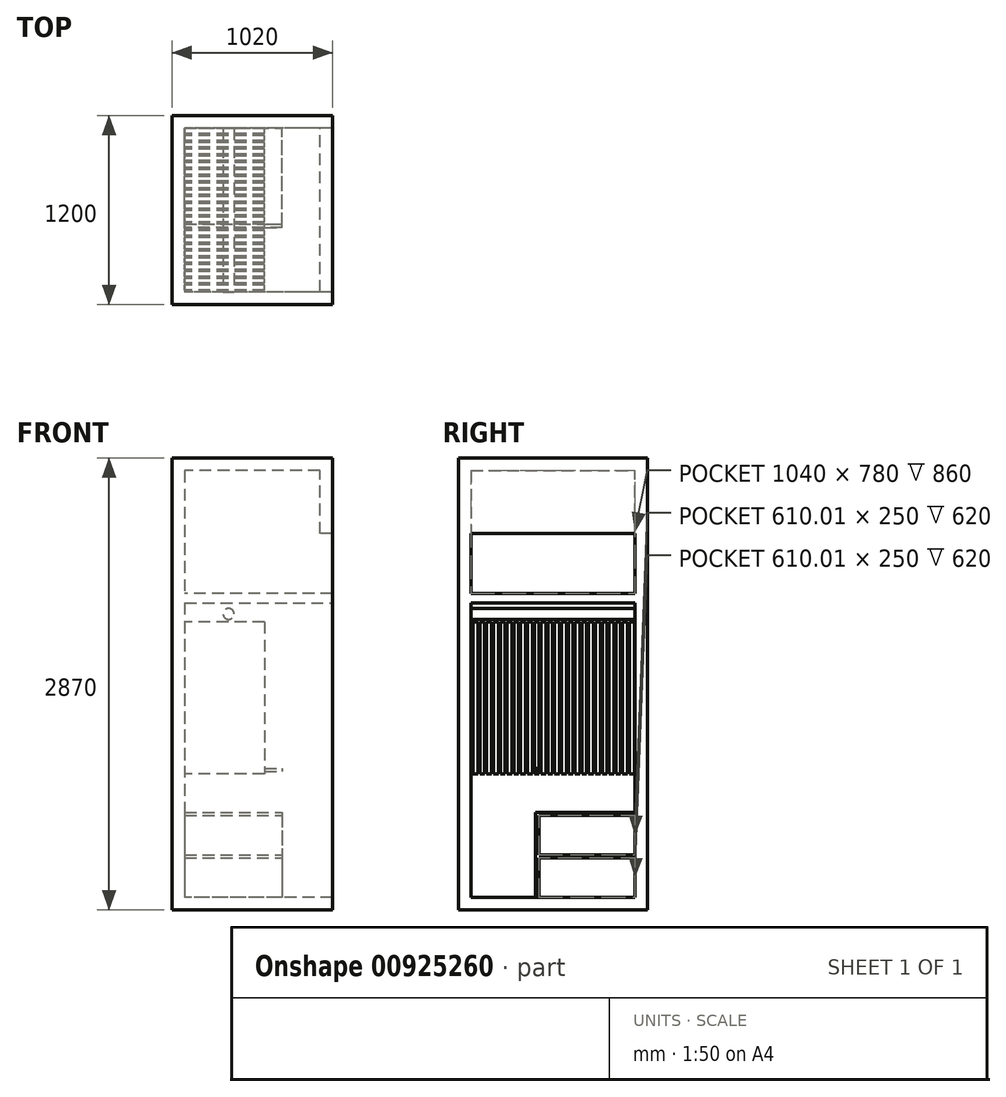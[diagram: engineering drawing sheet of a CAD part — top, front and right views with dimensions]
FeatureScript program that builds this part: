
annotation { "Feature Type Name" : "Feature", "Feature Type Description" : "" }
export const myFeature = defineFeature(function(context is Context, id is Id, definition is map)
    precondition{}
    {
        {
            var Q0;
            Q0=qCreatedBy(makeId("Top.planeOp"),FACE);
            var sketch = newSketch(context, id + "F0", { "sketchPlane" : qUnion([Q0])});
            skLineSegment(sketch, "E0.bottom", {"start": v(510, 600) * mm, "end": v(-510, 600) * mm});
            skLineSegment(sketch, "E0.top", {"start": v(510, -600) * mm, "end": v(-510, -600) * mm});
            skLineSegment(sketch, "E0.left", {"start": v(510, 600) * mm, "end": v(510, -600) * mm});
            skLineSegment(sketch, "E0.right", {"start": v(-510, 600) * mm, "end": v(-510, -600) * mm});
            skPoint(sketch, "E0.middle", {"position": v(0, 0) * mm});
            skSolve(sketch);
        }
        {
            var Q0;
            Q0=makeQuery(id+"F0.imprint","IMPRINT",FACE,{"disambiguationData":[TD([[makeQuery(id+"F0.imprint","IMPRINT",EDGE,{"derivedFrom":sQuery(id+"F0.wireOp",EDGE,"E0.bottom")}),1.0]])]});
            extrude(context, id + "F1", {"entities" : qUnion([Q0]), "depth" : 2870 * mm, "offsetDistance" : 25.4 * mm});
        }
        {
            var Q0;
            Q0=makeQuery(id+"F1.opExtrude","SWEPT_FACE",FACE,{"disambiguationData":[OSD([sQuery(id+"F0.wireOp",EDGE,"E0.left")])]});
            shell(context, id + "F2", {"entities" : qUnion([Q0]), "thickness" : 80 * mm});
        }
        {
            var Q0;
            {var subQ0=sQuery(id+"F0.wireOp",EDGE,"E0.right");var subQ1=sQuery(id+"F0.wireOp",EDGE,"E0.left");var subQ2=sQuery(id+"F0.wireOp",EDGE,"E0.top");var subQ3=sQuery(id+"F0.wireOp",EDGE,"E0.bottom");Q0=makeQuery(id+"F2.opShell","OFFSET_FACE",FACE,{"disambiguationData":[OSD([subQ3,subQ2,subQ1,subQ0]),TDD([makeQuery(id+"F1.opExtrude","CAP_FACE",FACE,{"disambiguationData":[OSD([subQ3,subQ2,subQ1,subQ0])],"isStart":false})])]});}
            var sketch = newSketch(context, id + "F3", { "sketchPlane" : qUnion([Q0])});
            skLineSegment(sketch, "E1.bottom", {"start": v(510, 520) * mm, "end": v(430, 520) * mm});
            skLineSegment(sketch, "E1.top", {"start": v(510, -520) * mm, "end": v(430, -520) * mm});
            skLineSegment(sketch, "E1.left", {"start": v(510, 520) * mm, "end": v(510, -520) * mm});
            skLineSegment(sketch, "E1.right", {"start": v(430, 520) * mm, "end": v(430, -520) * mm});
            skSolve(sketch);
        }
        {
            var Q0;
            Q0=makeQuery(id+"F3.imprint","IMPRINT",FACE,{"disambiguationData":[TD([[makeQuery(id+"F3.imprint","IMPRINT",EDGE,{"derivedFrom":sQuery(id+"F3.wireOp",EDGE,"E1.bottom")}),1.0]])]});
            extrude(context, id + "F4", {"entities" : qUnion([Q0]), "operationType" : NewBodyOperationType.ADD, "depth" : 400 * mm, "offsetDistance" : 25.4 * mm});
        }
        {
            var Q0;
            Q0=makeQuery(id+"F2.opShell","OFFSET_FACE",FACE,{"disambiguationData":[OSD([sQuery(id+"F0.wireOp",EDGE,"E0.top")])]});
            var sketch = newSketch(context, id + "F5", { "sketchPlane" : qUnion([Q0])});
            skLineSegment(sketch, "E2", {"start": v(-510, 2010) * mm, "end": v(430, 2010) * mm});
            skLineSegment(sketch, "E3", {"start": v(430, 2010) * mm, "end": v(430, 1950) * mm});
            skLineSegment(sketch, "E4", {"start": v(430, 1950) * mm, "end": v(-510, 1950) * mm});
            skLineSegment(sketch, "E5", {"start": v(-510, 1950) * mm, "end": v(-510, 2010) * mm});
            skSolve(sketch);
        }
        {
            var Q0;
            Q0=makeQuery(id+"F5.imprint","IMPRINT",FACE,{"disambiguationData":[TD([[makeQuery(id+"F5.imprint","IMPRINT",EDGE,{"derivedFrom":sQuery(id+"F5.wireOp",EDGE,"E2")}),-1.0]])]});
            extrude(context, id + "F6", {"entities" : qUnion([Q0]), "operationType" : NewBodyOperationType.ADD, "depth" : 1066.8 * mm, "offsetDistance" : 25.4 * mm});
        }
        {
            var Q0;
            {var subQ3=sQuery(id+"F0.wireOp",EDGE,"E0.bottom");Q0=makeQuery(id+"F6.boolean.opBoolean","SPLIT",FACE,{"disambiguationData":[TD([makeQuery(id+"F6.opExtrude","SWEPT_FACE",FACE,{"disambiguationData":[OSD([sQuery(id+"F5.wireOp",EDGE,"E4")])]})])],"derivedFrom":makeQuery(id+"F2.opShell","OFFSET_FACE",FACE,{"disambiguationData":[OSD([subQ3])]})});}
            var sketch = newSketch(context, id + "F7", { "sketchPlane" : qUnion([Q0])});
            skLineSegment(sketch, "E6.bottom", {"start": v(-430, 900) * mm, "end": v(190, 900) * mm});
            skLineSegment(sketch, "E6.top", {"start": v(-430, 80) * mm, "end": v(190, 80) * mm});
            skLineSegment(sketch, "E6.left", {"start": v(-430, 900) * mm, "end": v(-430, 80) * mm});
            skLineSegment(sketch, "E6.right", {"start": v(190, 900) * mm, "end": v(190, 80) * mm});
            skSolve(sketch);
        }
        {
            var Q0;
            Q0=makeQuery(id+"F7.imprint","IMPRINT",FACE,{"disambiguationData":[TD([[makeQuery(id+"F7.imprint","IMPRINT",EDGE,{"derivedFrom":sQuery(id+"F7.wireOp",EDGE,"E6.bottom")}),-1.0]])]});
            extrude(context, id + "F8", {"entities" : qUnion([Q0]), "operationType" : NewBodyOperationType.ADD, "depth" : 630 * mm, "offsetDistance" : 25.4 * mm});
        }
        {
            var Q0;
            Q0=makeQuery(id+"F8.opExtrude","SWEPT_FACE",FACE,{"disambiguationData":[OSD([sQuery(id+"F7.wireOp",EDGE,"E6.right")])]});
            var sketch = newSketch(context, id + "F9", { "sketchPlane" : qUnion([Q0])});
            skLineSegment(sketch, "E7.bottom", {"start": v(-110, 880) * mm, "end": v(520, 880) * mm});
            skLineSegment(sketch, "E7.top", {"start": v(-110, 620) * mm, "end": v(520, 620) * mm});
            skLineSegment(sketch, "E7.left", {"start": v(-110, 880) * mm, "end": v(-110, 620) * mm});
            skLineSegment(sketch, "E7.right", {"start": v(520, 880) * mm, "end": v(520, 620) * mm});
            skLineSegment(sketch, "E8.bottom", {"start": v(-110, 600) * mm, "end": v(520, 600) * mm});
            skLineSegment(sketch, "E8.top", {"start": v(-110, 350) * mm, "end": v(520, 350) * mm});
            skLineSegment(sketch, "E8.left", {"start": v(-110, 600) * mm, "end": v(-110, 350) * mm});
            skLineSegment(sketch, "E8.right", {"start": v(520, 600) * mm, "end": v(520, 350) * mm});
            skLineSegment(sketch, "E9.bottom", {"start": v(-110, 330) * mm, "end": v(520, 330) * mm});
            skLineSegment(sketch, "E9.top", {"start": v(-110, 80) * mm, "end": v(520, 80) * mm});
            skLineSegment(sketch, "E9.left", {"start": v(-110, 330) * mm, "end": v(-110, 80) * mm});
            skLineSegment(sketch, "E9.right", {"start": v(520, 330) * mm, "end": v(520, 80) * mm});
            skLineSegment(sketch, "E10", {"start": v(-90.01, 900) * mm, "end": v(-90.01, 80) * mm});
            skSolve(sketch);
        }
        {
            var Q0;
            {var subQ0=sQuery(id+"F9.wireOp",EDGE,"E7.right");Q0=makeQuery(id+"F9.imprint","IMPRINT",FACE,{"disambiguationData":[TD([[makeQuery(id+"F9.imprint","IMPRINT",EDGE,{"derivedFrom":subQ0}),-1.0]])]});}
            var Q1;
            {var subQ0=sQuery(id+"F9.wireOp",EDGE,"E8.right");Q1=makeQuery(id+"F9.imprint","IMPRINT",FACE,{"disambiguationData":[TD([[makeQuery(id+"F9.imprint","IMPRINT",EDGE,{"derivedFrom":subQ0}),-1.0]])]});}
            var Q2;
            {var subQ0=sQuery(id+"F9.wireOp",EDGE,"E9.right");Q2=makeQuery(id+"F9.imprint","IMPRINT",FACE,{"disambiguationData":[TD([[makeQuery(id+"F9.imprint","IMPRINT",EDGE,{"derivedFrom":subQ0}),-1.0]])]});}
            extrude(context, id + "F10", {"entities" : qUnion([Q0, Q1, Q2]), "operationType" : NewBodyOperationType.REMOVE, "oppositeDirection" : true, "depth" : 620 * mm, "offsetDistance" : 25.4 * mm});
        }
        {
            var Q0;
            {var subQ2=sQuery(id+"F0.wireOp",EDGE,"E0.top");Q0=makeQuery(id+"F6.boolean.opBoolean","SPLIT",FACE,{"disambiguationData":[TD([makeQuery(id+"F6.opExtrude","SWEPT_FACE",FACE,{"disambiguationData":[OSD([sQuery(id+"F5.wireOp",EDGE,"E4")])]})])],"derivedFrom":makeQuery(id+"F2.opShell","OFFSET_FACE",FACE,{"disambiguationData":[OSD([subQ2])]})});}
            var sketch = newSketch(context, id + "F11", { "sketchPlane" : qUnion([Q0])});
            skCircle(sketch, "E11", {"center": v(150, 1880) * mm, "radius": 35 * mm});
            skSolve(sketch);
        }
        {
            var Q0;
            Q0=makeQuery(id+"F11.imprint","IMPRINT",FACE,{"disambiguationData":[TD([[makeQuery(id+"F11.imprint","IMPRINT",EDGE,{"derivedFrom":sQuery(id+"F11.wireOp",EDGE,"E11")}),1.0]])]});
            var Q1;
            Q1=sQuery(id+"F11.wireOp",EDGE,"E11");
            extrude(context, id + "F12", {"entities" : qUnion([Q0]), "operationType" : NewBodyOperationType.ADD, "surfaceEntities" : qUnion([Q1]), "depth" : 1066.8 * mm, "offsetDistance" : 25.4 * mm});
        }
        {
            var Q0;
            Q0=makeQuery(id+"F8.opExtrude","SWEPT_FACE",FACE,{"disambiguationData":[OSD([sQuery(id+"F7.wireOp",EDGE,"E6.right")])]});
            var sketch = newSketch(context, id + "F13", { "sketchPlane" : qUnion([Q0])});
            skLineSegment(sketch, "E12.bottom", {"start": v(-90.01, 620) * mm, "end": v(-110, 620) * mm});
            skLineSegment(sketch, "E12.top", {"start": v(-90.01, 900) * mm, "end": v(-110, 900) * mm});
            skLineSegment(sketch, "E12.left", {"start": v(-90.01, 620) * mm, "end": v(-90.01, 900) * mm});
            skLineSegment(sketch, "E12.right", {"start": v(-110, 620) * mm, "end": v(-110, 900) * mm});
            skLineSegment(sketch, "E13.bottom", {"start": v(520, 880) * mm, "end": v(-110, 880) * mm});
            skLineSegment(sketch, "E13.top", {"start": v(520, 900) * mm, "end": v(-110, 900) * mm});
            skLineSegment(sketch, "E13.left", {"start": v(520, 880) * mm, "end": v(520, 900) * mm});
            skLineSegment(sketch, "E13.right", {"start": v(-110, 880) * mm, "end": v(-110, 900) * mm});
            skSolve(sketch);
        }
        {
            var Q0;
            {var subQ0=sQuery(id+"F13.wireOp",EDGE,"E12.bottom");Q0=makeQuery(id+"F13.imprint","IMPRINT",FACE,{"disambiguationData":[TD([[makeQuery(id+"F13.imprint","IMPRINT",EDGE,{"derivedFrom":subQ0}),-1.0]])]});}
            var Q1;
            {var subQ5=sQuery(id+"F13.wireOp",EDGE,"E13.left");Q1=makeQuery(id+"F13.imprint","IMPRINT",FACE,{"disambiguationData":[TD([[makeQuery(id+"F13.imprint","IMPRINT",EDGE,{"derivedFrom":subQ5}),-1.0]])]});}
            var Q2;
            {var subQ5=sQuery(id+"F13.wireOp",EDGE,"E13.right");Q2=makeQuery(id+"F13.imprint","IMPRINT",FACE,{"disambiguationData":[TD([[makeQuery(id+"F13.imprint","IMPRINT",EDGE,{"derivedFrom":subQ5}),1.0]])]});}
            extrude(context, id + "F14", {"entities" : qUnion([Q0, Q1, Q2]), "operationType" : NewBodyOperationType.REMOVE, "oppositeDirection" : true, "depth" : 620 * mm, "offsetDistance" : 25.4 * mm});
        }
        {
            var Q0;
            {var subQ1=sQuery(id+"F0.wireOp",EDGE,"E0.right");Q0=makeQuery(id+"F6.boolean.opBoolean","SPLIT",FACE,{"disambiguationData":[TD([makeQuery(id+"F6.opExtrude","SWEPT_FACE",FACE,{"disambiguationData":[OSD([sQuery(id+"F5.wireOp",EDGE,"E4")])]})])],"derivedFrom":makeQuery(id+"F2.opShell","OFFSET_FACE",FACE,{"disambiguationData":[OSD([subQ1])]})});}
            var sketch = newSketch(context, id + "F15", { "sketchPlane" : qUnion([Q0])});
            skLineSegment(sketch, "E14.bottom", {"start": v(-507.3, 1830) * mm, "end": v(-476.82, 1830) * mm});
            skLineSegment(sketch, "E14.top", {"start": v(-507.3, 864.8) * mm, "end": v(-476.82, 864.8) * mm});
            skLineSegment(sketch, "E14.left", {"start": v(-507.3, 1830) * mm, "end": v(-507.3, 864.8) * mm});
            skLineSegment(sketch, "E14.right", {"start": v(-476.82, 1830) * mm, "end": v(-476.82, 864.8) * mm});
            skLineSegment(sketch, "E15.bottom", {"start": v(-464.12, 1830) * mm, "end": v(-433.64, 1830) * mm});
            skLineSegment(sketch, "E15.top", {"start": v(-464.12, 864.8) * mm, "end": v(-433.64, 864.8) * mm});
            skLineSegment(sketch, "E15.left", {"start": v(-464.12, 1830) * mm, "end": v(-464.12, 864.8) * mm});
            skLineSegment(sketch, "E15.right", {"start": v(-433.64, 1830) * mm, "end": v(-433.64, 864.8) * mm});
            skLineSegment(sketch, "E16.bottom", {"start": v(-420.94, 1830) * mm, "end": v(-390.46, 1830) * mm});
            skLineSegment(sketch, "E16.top", {"start": v(-420.94, 864.8) * mm, "end": v(-390.46, 864.8) * mm});
            skLineSegment(sketch, "E16.left", {"start": v(-420.94, 1830) * mm, "end": v(-420.94, 864.8) * mm});
            skLineSegment(sketch, "E16.right", {"start": v(-390.46, 1830) * mm, "end": v(-390.46, 864.8) * mm});
            skLineSegment(sketch, "E17.bottom", {"start": v(-377.76, 1830) * mm, "end": v(-347.28, 1830) * mm});
            skLineSegment(sketch, "E17.top", {"start": v(-377.76, 864.8) * mm, "end": v(-347.28, 864.8) * mm});
            skLineSegment(sketch, "E17.left", {"start": v(-377.76, 1830) * mm, "end": v(-377.76, 864.8) * mm});
            skLineSegment(sketch, "E17.right", {"start": v(-347.28, 1830) * mm, "end": v(-347.28, 864.8) * mm});
            skLineSegment(sketch, "E18.bottom", {"start": v(-334.58, 1830) * mm, "end": v(-304.1, 1830) * mm});
            skLineSegment(sketch, "E18.top", {"start": v(-334.58, 864.8) * mm, "end": v(-304.1, 864.8) * mm});
            skLineSegment(sketch, "E18.left", {"start": v(-334.58, 1830) * mm, "end": v(-334.58, 864.8) * mm});
            skLineSegment(sketch, "E18.right", {"start": v(-304.1, 1830) * mm, "end": v(-304.1, 864.8) * mm});
            skLineSegment(sketch, "E19.bottom", {"start": v(-291.4, 1830) * mm, "end": v(-260.92, 1830) * mm});
            skLineSegment(sketch, "E19.top", {"start": v(-291.4, 864.8) * mm, "end": v(-260.92, 864.8) * mm});
            skLineSegment(sketch, "E19.left", {"start": v(-291.4, 1830) * mm, "end": v(-291.4, 864.8) * mm});
            skLineSegment(sketch, "E19.right", {"start": v(-260.92, 1830) * mm, "end": v(-260.92, 864.8) * mm});
            skLineSegment(sketch, "E20.bottom", {"start": v(-248.22, 1830) * mm, "end": v(-217.74, 1830) * mm});
            skLineSegment(sketch, "E20.top", {"start": v(-248.22, 864.8) * mm, "end": v(-217.74, 864.8) * mm});
            skLineSegment(sketch, "E20.left", {"start": v(-248.22, 1830) * mm, "end": v(-248.22, 864.8) * mm});
            skLineSegment(sketch, "E20.right", {"start": v(-217.74, 1830) * mm, "end": v(-217.74, 864.8) * mm});
            skLineSegment(sketch, "E21.bottom", {"start": v(-205.04, 1830) * mm, "end": v(-174.56, 1830) * mm});
            skLineSegment(sketch, "E21.top", {"start": v(-205.04, 864.8) * mm, "end": v(-174.56, 864.8) * mm});
            skLineSegment(sketch, "E21.left", {"start": v(-205.04, 1830) * mm, "end": v(-205.04, 864.8) * mm});
            skLineSegment(sketch, "E21.right", {"start": v(-174.56, 1830) * mm, "end": v(-174.56, 864.8) * mm});
            skLineSegment(sketch, "E22.bottom", {"start": v(-161.86, 1830) * mm, "end": v(-131.38, 1830) * mm});
            skLineSegment(sketch, "E22.top", {"start": v(-161.86, 864.8) * mm, "end": v(-131.38, 864.8) * mm});
            skLineSegment(sketch, "E22.left", {"start": v(-161.86, 1830) * mm, "end": v(-161.86, 864.8) * mm});
            skLineSegment(sketch, "E22.right", {"start": v(-131.38, 1830) * mm, "end": v(-131.38, 864.8) * mm});
            skLineSegment(sketch, "E23.bottom", {"start": v(-118.68, 1830) * mm, "end": v(-88.2, 1830) * mm});
            skLineSegment(sketch, "E23.top", {"start": v(-118.68, 864.8) * mm, "end": v(-88.2, 864.8) * mm});
            skLineSegment(sketch, "E23.left", {"start": v(-118.68, 1830) * mm, "end": v(-118.68, 864.8) * mm});
            skLineSegment(sketch, "E23.right", {"start": v(-88.2, 1830) * mm, "end": v(-88.2, 864.8) * mm});
            skLineSegment(sketch, "E24.bottom", {"start": v(-75.5, 1830) * mm, "end": v(-45.02, 1830) * mm});
            skLineSegment(sketch, "E24.top", {"start": v(-75.5, 864.8) * mm, "end": v(-45.02, 864.8) * mm});
            skLineSegment(sketch, "E24.left", {"start": v(-75.5, 1830) * mm, "end": v(-75.5, 864.8) * mm});
            skLineSegment(sketch, "E24.right", {"start": v(-45.02, 1830) * mm, "end": v(-45.02, 864.8) * mm});
            skLineSegment(sketch, "E25.bottom", {"start": v(-32.32, 1830) * mm, "end": v(-1.84, 1830) * mm});
            skLineSegment(sketch, "E25.top", {"start": v(-32.32, 864.8) * mm, "end": v(-1.84, 864.8) * mm});
            skLineSegment(sketch, "E25.left", {"start": v(-32.32, 1830) * mm, "end": v(-32.32, 864.8) * mm});
            skLineSegment(sketch, "E25.right", {"start": v(-1.84, 1830) * mm, "end": v(-1.84, 864.8) * mm});
            skLineSegment(sketch, "E26.bottom", {"start": v(10.86, 1830) * mm, "end": v(41.34, 1830) * mm});
            skLineSegment(sketch, "E26.top", {"start": v(10.86, 864.8) * mm, "end": v(41.34, 864.8) * mm});
            skLineSegment(sketch, "E26.left", {"start": v(10.86, 1830) * mm, "end": v(10.86, 864.8) * mm});
            skLineSegment(sketch, "E26.right", {"start": v(41.34, 1830) * mm, "end": v(41.34, 864.8) * mm});
            skLineSegment(sketch, "E27.bottom", {"start": v(54.04, 1830) * mm, "end": v(84.52, 1830) * mm});
            skLineSegment(sketch, "E27.top", {"start": v(54.04, 864.8) * mm, "end": v(84.52, 864.8) * mm});
            skLineSegment(sketch, "E27.left", {"start": v(54.04, 1830) * mm, "end": v(54.04, 864.8) * mm});
            skLineSegment(sketch, "E27.right", {"start": v(84.52, 1830) * mm, "end": v(84.52, 864.8) * mm});
            skLineSegment(sketch, "E28.bottom", {"start": v(97.22, 1830) * mm, "end": v(127.7, 1830) * mm});
            skLineSegment(sketch, "E28.top", {"start": v(97.22, 864.8) * mm, "end": v(127.7, 864.8) * mm});
            skLineSegment(sketch, "E28.left", {"start": v(97.22, 1830) * mm, "end": v(97.22, 864.8) * mm});
            skLineSegment(sketch, "E28.right", {"start": v(127.7, 1830) * mm, "end": v(127.7, 864.8) * mm});
            skLineSegment(sketch, "E29.bottom", {"start": v(140.4, 1830) * mm, "end": v(170.88, 1830) * mm});
            skLineSegment(sketch, "E29.top", {"start": v(140.4, 864.8) * mm, "end": v(170.88, 864.8) * mm});
            skLineSegment(sketch, "E29.left", {"start": v(140.4, 1830) * mm, "end": v(140.4, 864.8) * mm});
            skLineSegment(sketch, "E29.right", {"start": v(170.88, 1830) * mm, "end": v(170.88, 864.8) * mm});
            skLineSegment(sketch, "E30.bottom", {"start": v(183.58, 1830) * mm, "end": v(214.06, 1830) * mm});
            skLineSegment(sketch, "E30.top", {"start": v(183.58, 864.8) * mm, "end": v(214.06, 864.8) * mm});
            skLineSegment(sketch, "E30.left", {"start": v(183.58, 1830) * mm, "end": v(183.58, 864.8) * mm});
            skLineSegment(sketch, "E30.right", {"start": v(214.06, 1830) * mm, "end": v(214.06, 864.8) * mm});
            skLineSegment(sketch, "E31.bottom", {"start": v(226.76, 1830) * mm, "end": v(257.24, 1830) * mm});
            skLineSegment(sketch, "E31.top", {"start": v(226.76, 864.8) * mm, "end": v(257.24, 864.8) * mm});
            skLineSegment(sketch, "E31.left", {"start": v(226.76, 1830) * mm, "end": v(226.76, 864.8) * mm});
            skLineSegment(sketch, "E31.right", {"start": v(257.24, 1830) * mm, "end": v(257.24, 864.8) * mm});
            skLineSegment(sketch, "E32.bottom", {"start": v(269.94, 1830) * mm, "end": v(300.42, 1830) * mm});
            skLineSegment(sketch, "E32.top", {"start": v(269.94, 864.8) * mm, "end": v(300.42, 864.8) * mm});
            skLineSegment(sketch, "E32.left", {"start": v(269.94, 1830) * mm, "end": v(269.94, 864.8) * mm});
            skLineSegment(sketch, "E32.right", {"start": v(300.42, 1830) * mm, "end": v(300.42, 864.8) * mm});
            skLineSegment(sketch, "E33.bottom", {"start": v(313.12, 1830) * mm, "end": v(343.6, 1830) * mm});
            skLineSegment(sketch, "E33.top", {"start": v(313.12, 864.8) * mm, "end": v(343.6, 864.8) * mm});
            skLineSegment(sketch, "E33.left", {"start": v(313.12, 1830) * mm, "end": v(313.12, 864.8) * mm});
            skLineSegment(sketch, "E33.right", {"start": v(343.6, 1830) * mm, "end": v(343.6, 864.8) * mm});
            skLineSegment(sketch, "E34.bottom", {"start": v(356.3, 1830) * mm, "end": v(386.78, 1830) * mm});
            skLineSegment(sketch, "E34.top", {"start": v(356.3, 864.8) * mm, "end": v(386.78, 864.8) * mm});
            skLineSegment(sketch, "E34.left", {"start": v(356.3, 1830) * mm, "end": v(356.3, 864.8) * mm});
            skLineSegment(sketch, "E34.right", {"start": v(386.78, 1830) * mm, "end": v(386.78, 864.8) * mm});
            skLineSegment(sketch, "E35.bottom", {"start": v(399.48, 1830) * mm, "end": v(429.96, 1830) * mm});
            skLineSegment(sketch, "E35.top", {"start": v(399.48, 864.8) * mm, "end": v(429.96, 864.8) * mm});
            skLineSegment(sketch, "E35.left", {"start": v(399.48, 1830) * mm, "end": v(399.48, 864.8) * mm});
            skLineSegment(sketch, "E35.right", {"start": v(429.96, 1830) * mm, "end": v(429.96, 864.8) * mm});
            skLineSegment(sketch, "E36.bottom", {"start": v(442.66, 1830) * mm, "end": v(473.14, 1830) * mm});
            skLineSegment(sketch, "E36.top", {"start": v(442.66, 864.8) * mm, "end": v(473.14, 864.8) * mm});
            skLineSegment(sketch, "E36.left", {"start": v(442.66, 1830) * mm, "end": v(442.66, 864.8) * mm});
            skLineSegment(sketch, "E36.right", {"start": v(473.14, 1830) * mm, "end": v(473.14, 864.8) * mm});
            skLineSegment(sketch, "E37.bottom", {"start": v(485.84, 1830) * mm, "end": v(516.32, 1830) * mm});
            skLineSegment(sketch, "E37.top", {"start": v(485.84, 864.8) * mm, "end": v(516.32, 864.8) * mm});
            skLineSegment(sketch, "E37.left", {"start": v(485.84, 1830) * mm, "end": v(485.84, 864.8) * mm});
            skLineSegment(sketch, "E37.right", {"start": v(516.32, 1830) * mm, "end": v(516.32, 864.8) * mm});
            skSolve(sketch);
        }
        {
            var Q0;
            Q0=makeQuery(id+"F15.imprint","IMPRINT",FACE,{"disambiguationData":[TD([[makeQuery(id+"F15.imprint","IMPRINT",EDGE,{"derivedFrom":sQuery(id+"F15.wireOp",EDGE,"E14.bottom")}),-1.0]])]});
            var Q1;
            Q1=makeQuery(id+"F15.imprint","IMPRINT",FACE,{"disambiguationData":[TD([[makeQuery(id+"F15.imprint","IMPRINT",EDGE,{"derivedFrom":sQuery(id+"F15.wireOp",EDGE,"E15.bottom")}),-1.0]])]});
            var Q2;
            Q2=makeQuery(id+"F15.imprint","IMPRINT",FACE,{"disambiguationData":[TD([[makeQuery(id+"F15.imprint","IMPRINT",EDGE,{"derivedFrom":sQuery(id+"F15.wireOp",EDGE,"E16.bottom")}),-1.0]])]});
            var Q3;
            Q3=makeQuery(id+"F15.imprint","IMPRINT",FACE,{"disambiguationData":[TD([[makeQuery(id+"F15.imprint","IMPRINT",EDGE,{"derivedFrom":sQuery(id+"F15.wireOp",EDGE,"E17.bottom")}),-1.0]])]});
            var Q4;
            Q4=makeQuery(id+"F15.imprint","IMPRINT",FACE,{"disambiguationData":[TD([[makeQuery(id+"F15.imprint","IMPRINT",EDGE,{"derivedFrom":sQuery(id+"F15.wireOp",EDGE,"E18.bottom")}),-1.0]])]});
            var Q5;
            Q5=makeQuery(id+"F15.imprint","IMPRINT",FACE,{"disambiguationData":[TD([[makeQuery(id+"F15.imprint","IMPRINT",EDGE,{"derivedFrom":sQuery(id+"F15.wireOp",EDGE,"E19.bottom")}),-1.0]])]});
            var Q6;
            Q6=makeQuery(id+"F15.imprint","IMPRINT",FACE,{"disambiguationData":[TD([[makeQuery(id+"F15.imprint","IMPRINT",EDGE,{"derivedFrom":sQuery(id+"F15.wireOp",EDGE,"E20.bottom")}),-1.0]])]});
            var Q7;
            Q7=makeQuery(id+"F15.imprint","IMPRINT",FACE,{"disambiguationData":[TD([[makeQuery(id+"F15.imprint","IMPRINT",EDGE,{"derivedFrom":sQuery(id+"F15.wireOp",EDGE,"E21.bottom")}),-1.0]])]});
            var Q8;
            Q8=makeQuery(id+"F15.imprint","IMPRINT",FACE,{"disambiguationData":[TD([[makeQuery(id+"F15.imprint","IMPRINT",EDGE,{"derivedFrom":sQuery(id+"F15.wireOp",EDGE,"E22.bottom")}),-1.0]])]});
            var Q9;
            Q9=makeQuery(id+"F15.imprint","IMPRINT",FACE,{"disambiguationData":[TD([[makeQuery(id+"F15.imprint","IMPRINT",EDGE,{"derivedFrom":sQuery(id+"F15.wireOp",EDGE,"E23.bottom")}),-1.0]])]});
            var Q10;
            Q10=makeQuery(id+"F15.imprint","IMPRINT",FACE,{"disambiguationData":[TD([[makeQuery(id+"F15.imprint","IMPRINT",EDGE,{"derivedFrom":sQuery(id+"F15.wireOp",EDGE,"E24.bottom")}),-1.0]])]});
            var Q11;
            Q11=makeQuery(id+"F15.imprint","IMPRINT",FACE,{"disambiguationData":[TD([[makeQuery(id+"F15.imprint","IMPRINT",EDGE,{"derivedFrom":sQuery(id+"F15.wireOp",EDGE,"E25.bottom")}),-1.0]])]});
            var Q12;
            Q12=makeQuery(id+"F15.imprint","IMPRINT",FACE,{"disambiguationData":[TD([[makeQuery(id+"F15.imprint","IMPRINT",EDGE,{"derivedFrom":sQuery(id+"F15.wireOp",EDGE,"E26.bottom")}),-1.0]])]});
            var Q13;
            Q13=makeQuery(id+"F15.imprint","IMPRINT",FACE,{"disambiguationData":[TD([[makeQuery(id+"F15.imprint","IMPRINT",EDGE,{"derivedFrom":sQuery(id+"F15.wireOp",EDGE,"E27.bottom")}),-1.0]])]});
            var Q14;
            Q14=makeQuery(id+"F15.imprint","IMPRINT",FACE,{"disambiguationData":[TD([[makeQuery(id+"F15.imprint","IMPRINT",EDGE,{"derivedFrom":sQuery(id+"F15.wireOp",EDGE,"E28.bottom")}),-1.0]])]});
            var Q15;
            Q15=makeQuery(id+"F15.imprint","IMPRINT",FACE,{"disambiguationData":[TD([[makeQuery(id+"F15.imprint","IMPRINT",EDGE,{"derivedFrom":sQuery(id+"F15.wireOp",EDGE,"E29.bottom")}),-1.0]])]});
            var Q16;
            Q16=makeQuery(id+"F15.imprint","IMPRINT",FACE,{"disambiguationData":[TD([[makeQuery(id+"F15.imprint","IMPRINT",EDGE,{"derivedFrom":sQuery(id+"F15.wireOp",EDGE,"E30.bottom")}),-1.0]])]});
            var Q17;
            Q17=makeQuery(id+"F15.imprint","IMPRINT",FACE,{"disambiguationData":[TD([[makeQuery(id+"F15.imprint","IMPRINT",EDGE,{"derivedFrom":sQuery(id+"F15.wireOp",EDGE,"E31.bottom")}),-1.0]])]});
            var Q18;
            Q18=makeQuery(id+"F15.imprint","IMPRINT",FACE,{"disambiguationData":[TD([[makeQuery(id+"F15.imprint","IMPRINT",EDGE,{"derivedFrom":sQuery(id+"F15.wireOp",EDGE,"E32.bottom")}),-1.0]])]});
            var Q19;
            Q19=makeQuery(id+"F15.imprint","IMPRINT",FACE,{"disambiguationData":[TD([[makeQuery(id+"F15.imprint","IMPRINT",EDGE,{"derivedFrom":sQuery(id+"F15.wireOp",EDGE,"E33.bottom")}),-1.0]])]});
            var Q20;
            Q20=makeQuery(id+"F15.imprint","IMPRINT",FACE,{"disambiguationData":[TD([[makeQuery(id+"F15.imprint","IMPRINT",EDGE,{"derivedFrom":sQuery(id+"F15.wireOp",EDGE,"E34.bottom")}),-1.0]])]});
            var Q21;
            Q21=makeQuery(id+"F15.imprint","IMPRINT",FACE,{"disambiguationData":[TD([[makeQuery(id+"F15.imprint","IMPRINT",EDGE,{"derivedFrom":sQuery(id+"F15.wireOp",EDGE,"E35.bottom")}),-1.0]])]});
            var Q22;
            Q22=makeQuery(id+"F15.imprint","IMPRINT",FACE,{"disambiguationData":[TD([[makeQuery(id+"F15.imprint","IMPRINT",EDGE,{"derivedFrom":sQuery(id+"F15.wireOp",EDGE,"E36.bottom")}),-1.0]])]});
            var Q23;
            Q23=makeQuery(id+"F15.imprint","IMPRINT",FACE,{"disambiguationData":[TD([[makeQuery(id+"F15.imprint","IMPRINT",EDGE,{"derivedFrom":sQuery(id+"F15.wireOp",EDGE,"E37.bottom")}),-1.0]])]});
            extrude(context, id + "F16", {"entities" : qUnion([Q0, Q1, Q2, Q3, Q4, Q5, Q6, Q7, Q8, Q9, Q10, Q11, Q12, Q13, Q14, Q15, Q16, Q17, Q18, Q19, Q20, Q21, Q22, Q23]), "operationType" : NewBodyOperationType.ADD, "depth" : 508 * mm, "offsetDistance" : 25.4 * mm});
        }
    });
